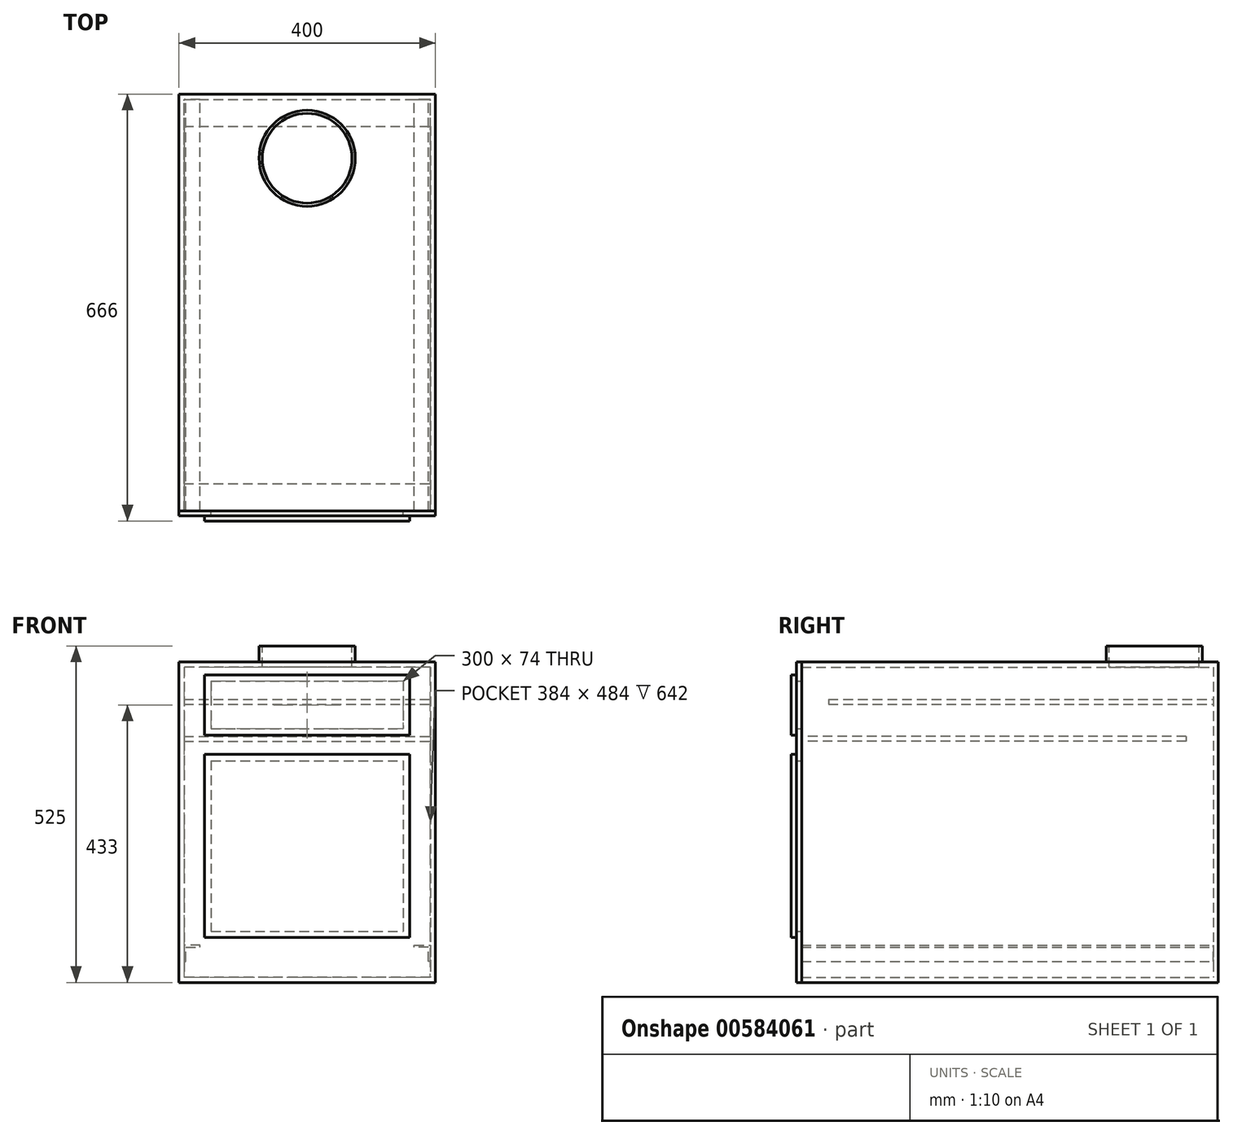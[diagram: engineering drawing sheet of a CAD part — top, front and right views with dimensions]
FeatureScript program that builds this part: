
annotation { "Feature Type Name" : "Feature", "Feature Type Description" : "" }
export const myFeature = defineFeature(function(context is Context, id is Id, definition is map)
    precondition{}
    {
        {
            assignVariable(context, id + "F0", {"name" : "Thickness", "anyValue" : 8});
        }
        {
            var Q0;
            Q0=qCreatedBy(makeId("Top.planeOp"),FACE);
            var sketch = newSketch(context, id + "F1", { "sketchPlane" : qUnion([Q0])});
            skLineSegment(sketch, "E0.bottom", {"start": v(200, 0) * mm, "end": v(-200, 0) * mm});
            skLineSegment(sketch, "E0.top", {"start": v(200, 650) * mm, "end": v(-200, 650) * mm});
            skLineSegment(sketch, "E0.left", {"start": v(200, 0) * mm, "end": v(200, 650) * mm});
            skLineSegment(sketch, "E0.right", {"start": v(-200, 0) * mm, "end": v(-200, 650) * mm});
            skPoint(sketch, "E0.middle", {"position": v(0, 325) * mm});
            skSolve(sketch);
        }
        {
            var Q0;
            Q0 = qSketchRegion(id + "F1", true);
            extrude(context, id + "F2", {"entities" : qUnion([Q0]), "depth" : 500 * mm, "offsetDistance" : 25 * mm});
        }
        {
            var Q0;
            Q0=makeQuery(id+"F2.opExtrude","SWEPT_FACE",FACE,{"disambiguationData":[OSD([sQuery(id+"F1.wireOp",EDGE,"E0.bottom")])]});
            var Q1;
            Q1=makeQuery(id+"F2.opExtrude","SWEPT_BODY",BODY,{"disambiguationData":[OSD([sQuery(id+"F1.wireOp",EDGE,"E0.bottom"),sQuery(id+"F1.wireOp",EDGE,"E0.top"),sQuery(id+"F1.wireOp",EDGE,"E0.left"),sQuery(id+"F1.wireOp",EDGE,"E0.right")])]});
            shell(context, id + "F3", {"entities" : qUnion([Q0]), "parts" : qUnion([Q1]), "thickness" : (getVariable(context, 'Thickness')) * mm});
        }
        {
            var Q0;
            Q0=makeQuery(id+"F3.opShell","OFFSET_FACE",FACE,{"disambiguationData":[OSD([sQuery(id+"F1.wireOp",EDGE,"E0.top")])]});
            var sketch = newSketch(context, id + "F4", { "sketchPlane" : qUnion([Q0])});
            skLineSegment(sketch, "E1.bottom", {"start": v(-192, 442) * mm, "end": v(192, 442) * mm});
            skLineSegment(sketch, "E1.top", {"start": v(-192, 434) * mm, "end": v(192, 434) * mm});
            skLineSegment(sketch, "E1.left", {"start": v(-192, 442) * mm, "end": v(-192, 434) * mm});
            skLineSegment(sketch, "E1.right", {"start": v(192, 442) * mm, "end": v(192, 434) * mm});
            skSolve(sketch);
        }
        {
            var Q0;
            Q0 = qSketchRegion(id + "F4", true);
            extrude(context, id + "F5", {"entities" : qUnion([Q0]), "depth" : 600 * mm, "offsetDistance" : 25 * mm});
        }
        {
            var Q0;
            Q0=makeQuery(id+"F2.opExtrude","SWEPT_FACE",FACE,{"disambiguationData":[OSD([sQuery(id+"F1.wireOp",EDGE,"E0.bottom")])]});
            var sketch = newSketch(context, id + "F6", { "sketchPlane" : qUnion([Q0])});
            skLineSegment(sketch, "E2.bottom", {"start": v(-192, 384) * mm, "end": v(192, 384) * mm});
            skLineSegment(sketch, "E2.top", {"start": v(-192, 376) * mm, "end": v(192, 376) * mm});
            skLineSegment(sketch, "E2.left", {"start": v(-192, 384) * mm, "end": v(-192, 376) * mm});
            skLineSegment(sketch, "E2.right", {"start": v(192, 384) * mm, "end": v(192, 376) * mm});
            skSolve(sketch);
        }
        {
            var Q0;
            Q0 = qSketchRegion(id + "F6", true);
            extrude(context, id + "F7", {"entities" : qUnion([Q0]), "oppositeDirection" : true, "depth" : 600 * mm, "offsetDistance" : 25 * mm});
        }
        {
            var Q0;
            Q0=makeQuery(id+"F3.opShell","OFFSET_FACE",FACE,{"disambiguationData":[OSD([sQuery(id+"F1.wireOp",EDGE,"E0.top")])]});
            var sketch = newSketch(context, id + "F8", { "sketchPlane" : qUnion([Q0])});
            skLineSegment(sketch, "E3", {"start": v(-167, 58) * mm, "end": v(-192, 58) * mm});
            skLineSegment(sketch, "E4", {"start": v(-192, 58) * mm, "end": v(-192, 33) * mm});
            skLineSegment(sketch, "E5", {"start": v(-192, 33) * mm, "end": v(-189, 33) * mm});
            skLineSegment(sketch, "E6", {"start": v(-189, 33) * mm, "end": v(-189, 55) * mm});
            skLineSegment(sketch, "E7", {"start": v(-189, 55) * mm, "end": v(-167, 55) * mm});
            skLineSegment(sketch, "E8", {"start": v(-167, 55) * mm, "end": v(-167, 58) * mm});
            skLineSegment(sketch, "E9.MirrorCS", {"start": v(192, 33) * mm, "end": v(189, 33) * mm});
            skLineSegment(sketch, "E10.MirrorCS", {"start": v(167, 55) * mm, "end": v(167, 58) * mm});
            skLineSegment(sketch, "E11.MirrorCS", {"start": v(192, 58) * mm, "end": v(192, 33) * mm});
            skLineSegment(sketch, "E12.MirrorCS", {"start": v(167, 58) * mm, "end": v(192, 58) * mm});
            skLineSegment(sketch, "E13.MirrorCS", {"start": v(189, 33) * mm, "end": v(189, 55) * mm});
            skLineSegment(sketch, "E14.MirrorCS", {"start": v(189, 55) * mm, "end": v(167, 55) * mm});
            skSolve(sketch);
        }
        {
            var Q0;
            Q0 = qSketchRegion(id + "F8", true);
            var Q1;
            Q1=makeQuery(id+"F2.opExtrude","SWEPT_FACE",FACE,{"disambiguationData":[OSD([sQuery(id+"F1.wireOp",EDGE,"E0.bottom")])]});
            extrude(context, id + "F9", {"entities" : qUnion([Q0]), "endBound" : BoundingType.UP_TO_SURFACE, "depth" : 25 * mm, "endBoundEntityFace" : qUnion([Q1]), "offsetDistance" : 25 * mm});
        }
        {
            var Q0;
            Q0=makeQuery(id+"F2.opExtrude","CAP_FACE",FACE,{"disambiguationData":[OSD([sQuery(id+"F1.wireOp",EDGE,"E0.bottom"),sQuery(id+"F1.wireOp",EDGE,"E0.top"),sQuery(id+"F1.wireOp",EDGE,"E0.left"),sQuery(id+"F1.wireOp",EDGE,"E0.right")])],"isStart":false});
            var sketch = newSketch(context, id + "F10", { "sketchPlane" : qUnion([Q0])});
            skCircle(sketch, "E15", {"center": v(0, 550) * mm, "radius": 75 * mm});
            skSolve(sketch);
        }
        {
            var Q0;
            Q0 = qSketchRegion(id + "F10", true);
            extrude(context, id + "F11", {"entities" : qUnion([Q0]), "operationType" : NewBodyOperationType.ADD, "depth" : 25 * mm, "offsetDistance" : 25 * mm});
        }
        {
            var Q0;
            Q0=makeQuery(id+"F11.opExtrude","CAP_FACE",FACE,{"disambiguationData":[OSD([sQuery(id+"F10.wireOp",EDGE,"E15")])],"isStart":false});
            var sketch = newSketch(context, id + "F12", { "sketchPlane" : qUnion([Q0])});
            skCircle(sketch, "E16", {"center": v(0, 550) * mm, "radius": 70 * mm});
            skSolve(sketch);
        }
        {
            var Q0;
            Q0 = qSketchRegion(id + "F12", true);
            extrude(context, id + "F13", {"entities" : qUnion([Q0]), "operationType" : NewBodyOperationType.REMOVE, "endBound" : BoundingType.UP_TO_NEXT, "oppositeDirection" : true, "depth" : 25 * mm, "offsetDistance" : 25 * mm});
        }
        {
            var Q0;
            Q0=makeQuery(id+"F2.opExtrude","SWEPT_FACE",FACE,{"disambiguationData":[OSD([sQuery(id+"F1.wireOp",EDGE,"E0.bottom")])]});
            var sketch = newSketch(context, id + "F14", { "sketchPlane" : qUnion([Q0])});
            skLineSegment(sketch, "E17.bottom", {"start": v(-200, 500) * mm, "end": v(200, 500) * mm});
            skLineSegment(sketch, "E17.top", {"start": v(-200, 0) * mm, "end": v(200, 0) * mm});
            skLineSegment(sketch, "E17.left", {"start": v(-200, 500) * mm, "end": v(-200, 0) * mm});
            skLineSegment(sketch, "E17.right", {"start": v(200, 500) * mm, "end": v(200, 0) * mm});
            skLineSegment(sketch, "E18.bottom", {"start": v(-150, 346) * mm, "end": v(150, 346) * mm});
            skLineSegment(sketch, "E18.top", {"start": v(-150, 80) * mm, "end": v(150, 80) * mm});
            skLineSegment(sketch, "E18.left", {"start": v(-150, 346) * mm, "end": v(-150, 80) * mm});
            skLineSegment(sketch, "E18.right", {"start": v(150, 346) * mm, "end": v(150, 80) * mm});
            skLineSegment(sketch, "E19.bottom", {"start": v(-150, 470) * mm, "end": v(150, 470) * mm});
            skLineSegment(sketch, "E19.top", {"start": v(-150, 396) * mm, "end": v(150, 396) * mm});
            skLineSegment(sketch, "E19.left", {"start": v(-150, 470) * mm, "end": v(-150, 396) * mm});
            skLineSegment(sketch, "E19.right", {"start": v(150, 470) * mm, "end": v(150, 396) * mm});
            skSolve(sketch);
        }
        {
            var Q0;
            Q0 = qSketchRegion(id + "F14", true);
            extrude(context, id + "F15", {"entities" : qUnion([Q0]), "depth" : (getVariable(context, 'Thickness')) * mm, "offsetDistance" : 25 * mm});
        }
        {
            var Q0;
            Q0=makeQuery(id+"F15.opExtrude","CAP_FACE",FACE,{"disambiguationData":[OSD([sQuery(id+"F14.wireOp",EDGE,"E17.bottom"),sQuery(id+"F14.wireOp",EDGE,"E17.top"),sQuery(id+"F14.wireOp",EDGE,"E17.left"),sQuery(id+"F14.wireOp",EDGE,"E17.right"),sQuery(id+"F14.wireOp",EDGE,"E18.bottom"),sQuery(id+"F14.wireOp",EDGE,"E18.top"),sQuery(id+"F14.wireOp",EDGE,"E18.left"),sQuery(id+"F14.wireOp",EDGE,"E18.right"),sQuery(id+"F14.wireOp",EDGE,"E19.bottom"),sQuery(id+"F14.wireOp",EDGE,"E19.top"),sQuery(id+"F14.wireOp",EDGE,"E19.left"),sQuery(id+"F14.wireOp",EDGE,"E19.right")])],"isStart":false});
            var sketch = newSketch(context, id + "F16", { "sketchPlane" : qUnion([Q0])});
            skLineSegment(sketch, "E20.bottom", {"start": v(-160, 480) * mm, "end": v(160, 480) * mm});
            skLineSegment(sketch, "E20.top", {"start": v(-160, 386) * mm, "end": v(160, 386) * mm});
            skLineSegment(sketch, "E20.left", {"start": v(-160, 480) * mm, "end": v(-160, 386) * mm});
            skLineSegment(sketch, "E20.right", {"start": v(160, 480) * mm, "end": v(160, 386) * mm});
            skLineSegment(sketch, "E21.bottom", {"start": v(-160, 356) * mm, "end": v(160, 356) * mm});
            skLineSegment(sketch, "E21.top", {"start": v(-160, 70) * mm, "end": v(160, 70) * mm});
            skLineSegment(sketch, "E21.left", {"start": v(-160, 356) * mm, "end": v(-160, 70) * mm});
            skLineSegment(sketch, "E21.right", {"start": v(160, 356) * mm, "end": v(160, 70) * mm});
            skSolve(sketch);
        }
        {
            var Q0;
            Q0 = qSketchRegion(id + "F16", true);
            extrude(context, id + "F17", {"entities" : qUnion([Q0]), "depth" : (getVariable(context, 'Thickness')) * mm, "offsetDistance" : 25 * mm});
        }
    });
